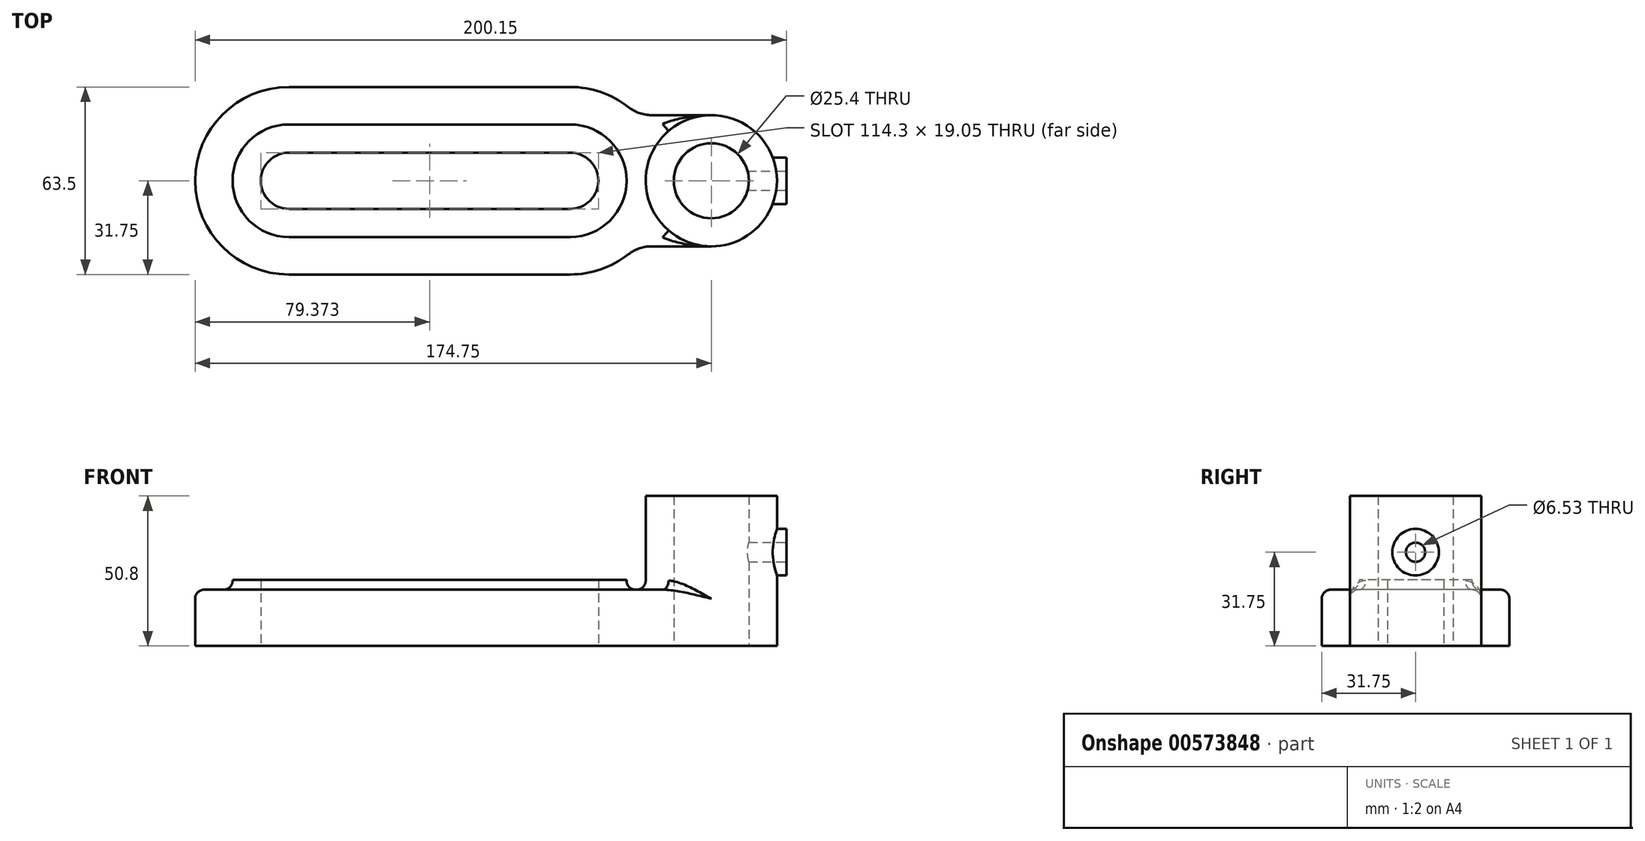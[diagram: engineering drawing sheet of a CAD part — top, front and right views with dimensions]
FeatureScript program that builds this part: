
annotation { "Feature Type Name" : "Feature", "Feature Type Description" : "" }
export const myFeature = defineFeature(function(context is Context, id is Id, definition is map)
    precondition{}
    {
        {
            var Q0;
            Q0=qCreatedBy(makeId("Top.planeOp"),FACE);
            var sketch = newSketch(context, id + "F0", { "sketchPlane" : qUnion([Q0])});
            skLineSegment(sketch, "E0", {"start": v(-143, 0) * mm, "end": v(-47.75, 0) * mm, "construction": true});
            skLineSegment(sketch, "E1", {"start": v(-47.75, 0) * mm, "end": v(0, 0) * mm, "construction": true});
            skLineSegment(sketch, "E2", {"start": v(0, 0) * mm, "end": v(25.4, 0) * mm, "construction": true});
            skLineSegment(sketch, "E3", {"start": v(0, 27.48) * mm, "end": v(0, -43.58) * mm, "construction": true});
            skLineSegment(sketch, "E4", {"start": v(-47.75, 38.75) * mm, "end": v(-47.75, -47.4) * mm, "construction": true});
            skLineSegment(sketch, "E5", {"start": v(-143, 39.55) * mm, "end": v(-143, -47.4) * mm, "construction": true});
            skArc(sketch, "E6", {"start": v(-143, 9.53) * mm, "mid": v(-152.53, 0) * mm, "end": v(-143, -9.53) * mm});
            skArc(sketch, "E7", {"start": v(-47.75, -9.53) * mm, "mid": v(-38.23, 0) * mm, "end": v(-47.75, 9.53) * mm});
            skCircle(sketch, "E8", {"center": v(0, 0) * mm, "radius": 12.7 * mm});
            skPoint(sketch, "E9", {"position": v(-143, 9.53) * mm});
            skPoint(sketch, "E10", {"position": v(-143, -9.53) * mm});
            skPoint(sketch, "E11", {"position": v(-47.75, 9.53) * mm});
            skPoint(sketch, "E12", {"position": v(-47.75, -9.52) * mm});
            skLineSegment(sketch, "E13", {"start": v(-143, 9.53) * mm, "end": v(-47.75, 9.53) * mm});
            skLineSegment(sketch, "E14", {"start": v(-47.75, -9.53) * mm, "end": v(-143, -9.53) * mm});
            skArc(sketch, "E15.0.startCap", {"start": v(-143, -19.05) * mm, "mid": v(-162.05, 0) * mm, "end": v(-143, 19.05) * mm});
            skArc(sketch, "E15.0.endCap", {"start": v(-47.75, 19.05) * mm, "mid": v(-28.7, 0) * mm, "end": v(-47.75, -19.05) * mm});
            skLineSegment(sketch, "E15.0.left", {"start": v(-143, 19.05) * mm, "end": v(-47.75, 19.05) * mm});
            skLineSegment(sketch, "E15.0.right", {"start": v(-143, -19.05) * mm, "end": v(-47.75, -19.05) * mm});
            skArc(sketch, "E16.0.startCap", {"start": v(-143, -31.75) * mm, "mid": v(-174.75, 0) * mm, "end": v(-143, 31.75) * mm});
            skArc(sketch, "E16.0.endCap", {"start": v(-47.75, 31.75) * mm, "mid": v(-37.36, 30) * mm, "end": v(-28.11, 24.95) * mm});
            skLineSegment(sketch, "E16.0.left", {"start": v(-143, 31.75) * mm, "end": v(-47.75, 31.75) * mm});
            skLineSegment(sketch, "E16.0.right", {"start": v(-143, -31.75) * mm, "end": v(-47.75, -31.75) * mm});
            skCircle(sketch, "E17", {"center": v(0, 0) * mm, "radius": 22.23 * mm});
            skLineSegment(sketch, "E18", {"start": v(0, 22.23) * mm, "end": v(-20.26, 22.23) * mm});
            skLineSegment(sketch, "E19", {"start": v(0, -22.23) * mm, "end": v(-20.26, -22.23) * mm});
            skArc(sketch, "E20.trimOffspring", {"start": v(-28.11, -24.95) * mm, "mid": v(-37.36, -30) * mm, "end": v(-47.75, -31.75) * mm});
            skPoint(sketch, "E21.visualSharp", {"position": v(-25.08, 22.23) * mm});
            skArc(sketch, "E21.filletArc", {"start": v(-28.11, 24.95) * mm, "mid": v(-24.41, 22.92) * mm, "end": v(-20.26, 22.23) * mm});
            skPoint(sketch, "E22.visualSharp", {"position": v(-25.08, -22.23) * mm});
            skArc(sketch, "E22.filletArc", {"start": v(-20.26, -22.23) * mm, "mid": v(-24.41, -22.92) * mm, "end": v(-28.11, -24.95) * mm});
            skSolve(sketch);
        }
        {
            var Q0;
            Q0=makeQuery(id+"F0.imprint","IMPRINT",FACE,{"disambiguationData":[TD([[makeQuery(id+"F0.imprint","IMPRINT",EDGE,{"derivedFrom":sQuery(id+"F0.wireOp",EDGE,"E8")}),-1.0]])]});
            extrude(context, id + "F1", {"entities" : qUnion([Q0]), "depth" : 50.8 * mm, "offsetDistance" : 25.4 * mm});
        }
        {
            var Q0;
            Q0 = qSketchRegion(id + "F0", true);
            var Q1;
            Q1=makeQuery(id+"F0.imprint","IMPRINT",FACE,{"disambiguationData":[TD([[makeQuery(id+"F0.imprint","IMPRINT",EDGE,{"derivedFrom":sQuery(id+"F0.wireOp",EDGE,"E6")}),-1.0]])]});
            extrude(context, id + "F2", {"entities" : qUnion([Q0, Q1]), "operationType" : NewBodyOperationType.ADD, "depth" : 19.05 * mm, "offsetDistance" : 25.4 * mm});
        }
        {
            var Q0;
            Q0=makeQuery(id+"F0.imprint","IMPRINT",FACE,{"disambiguationData":[TD([[makeQuery(id+"F0.imprint","IMPRINT",EDGE,{"derivedFrom":sQuery(id+"F0.wireOp",EDGE,"E6")}),-1.0]])]});
            extrude(context, id + "F3", {"entities" : qUnion([Q0]), "operationType" : NewBodyOperationType.ADD, "depth" : 22.35 * mm, "offsetDistance" : 25.4 * mm});
        }
        {
            var Q0;
            Q0=qCreatedBy(makeId("Right.planeOp"),FACE);
            cPlane(context, id + "F4", {"entities" : qUnion([Q0]), "cplaneType" : CPlaneType.OFFSET, "offset" : 25.4 * mm, "width" : 152.4 * mm, "height" : 152.4 * mm});
        }
        {
            var Q0;
            Q0=qCreatedBy(id+"F4.planeOp",FACE);
            var sketch = newSketch(context, id + "F5", { "sketchPlane" : qUnion([Q0])});
            skCircle(sketch, "E23", {"center": v(0, 31.75) * mm, "radius": 7.87 * mm});
            skCircle(sketch, "E24", {"center": v(0, 31.75) * mm, "radius": 3.26 * mm});
            skSolve(sketch);
        }
        {
            var Q0;
            Q0=makeQuery(id+"F5.imprint","IMPRINT",FACE,{"disambiguationData":[TD([[makeQuery(id+"F5.imprint","IMPRINT",EDGE,{"derivedFrom":sQuery(id+"F5.wireOp",EDGE,"E23")}),1.0]])]});
            extrude(context, id + "F6", {"entities" : qUnion([Q0]), "operationType" : NewBodyOperationType.ADD, "endBound" : BoundingType.UP_TO_NEXT, "oppositeDirection" : true, "depth" : 25.4 * mm, "offsetDistance" : 25.4 * mm});
        }
        {
            var Q0;
            Q0=makeQuery(id+"F5.imprint","IMPRINT",FACE,{"disambiguationData":[TD([[makeQuery(id+"F5.imprint","IMPRINT",EDGE,{"derivedFrom":sQuery(id+"F5.wireOp",EDGE,"E24")}),1.0]])]});
            extrude(context, id + "F7", {"entities" : qUnion([Q0]), "operationType" : NewBodyOperationType.REMOVE, "oppositeDirection" : true, "depth" : 25.4 * mm, "offsetDistance" : 25.4 * mm});
        }
        {
            var Q0;
            Q0=makeQuery(id+"F6.opExtrude","CAP_EDGE",EDGE,{"disambiguationData":[OSD([sQuery(id+"F5.wireOp",EDGE,"E23")])],"isStart":false});
            var Q1;
            Q1=makeQuery(id+"F3.boolean.opBoolean","INTERSECT",EDGE,{"derivedFrom":[makeQuery(id+"F2.opExtrude","CAP_FACE",FACE,{"disambiguationData":[OSD([sQuery(id+"F0.wireOp",EDGE,"E6"),sQuery(id+"F0.wireOp",EDGE,"E7"),sQuery(id+"F0.wireOp",EDGE,"E8"),sQuery(id+"F0.wireOp",EDGE,"E13"),sQuery(id+"F0.wireOp",EDGE,"E14"),sQuery(id+"F0.wireOp",EDGE,"E16.0.startCap"),sQuery(id+"F0.wireOp",EDGE,"E16.0.endCap"),sQuery(id+"F0.wireOp",EDGE,"E16.0.left"),sQuery(id+"F0.wireOp",EDGE,"E16.0.right"),sQuery(id+"F0.wireOp",EDGE,"E17"),sQuery(id+"F0.wireOp",EDGE,"E18"),sQuery(id+"F0.wireOp",EDGE,"E19"),sQuery(id+"F0.wireOp",EDGE,"E20.trimOffspring"),sQuery(id+"F0.wireOp",EDGE,"E21.filletArc"),sQuery(id+"F0.wireOp",EDGE,"E22.filletArc")])],"isStart":false}),makeQuery(id+"F3.opExtrude","SWEPT_FACE",FACE,{"disambiguationData":[OSD([sQuery(id+"F0.wireOp",EDGE,"E15.0.endCap")])]})]});
            var Q2;
            Q2=makeQuery(id+"F2.opExtrude","CAP_FACE",FACE,{"disambiguationData":[OSD([sQuery(id+"F0.wireOp",EDGE,"E6"),sQuery(id+"F0.wireOp",EDGE,"E7"),sQuery(id+"F0.wireOp",EDGE,"E8"),sQuery(id+"F0.wireOp",EDGE,"E13"),sQuery(id+"F0.wireOp",EDGE,"E14"),sQuery(id+"F0.wireOp",EDGE,"E16.0.startCap"),sQuery(id+"F0.wireOp",EDGE,"E16.0.endCap"),sQuery(id+"F0.wireOp",EDGE,"E16.0.left"),sQuery(id+"F0.wireOp",EDGE,"E16.0.right"),sQuery(id+"F0.wireOp",EDGE,"E17"),sQuery(id+"F0.wireOp",EDGE,"E18"),sQuery(id+"F0.wireOp",EDGE,"E19"),sQuery(id+"F0.wireOp",EDGE,"E20.trimOffspring"),sQuery(id+"F0.wireOp",EDGE,"E21.filletArc"),sQuery(id+"F0.wireOp",EDGE,"E22.filletArc")])],"isStart":false});
            fillet(context, id + "F8", {"entities" : qUnion([Q0, Q1, Q2]), "radius" : 3.05 * mm, "tangentPropagation" : true, "allowEdgeOverflow" : false});
        }
    });
